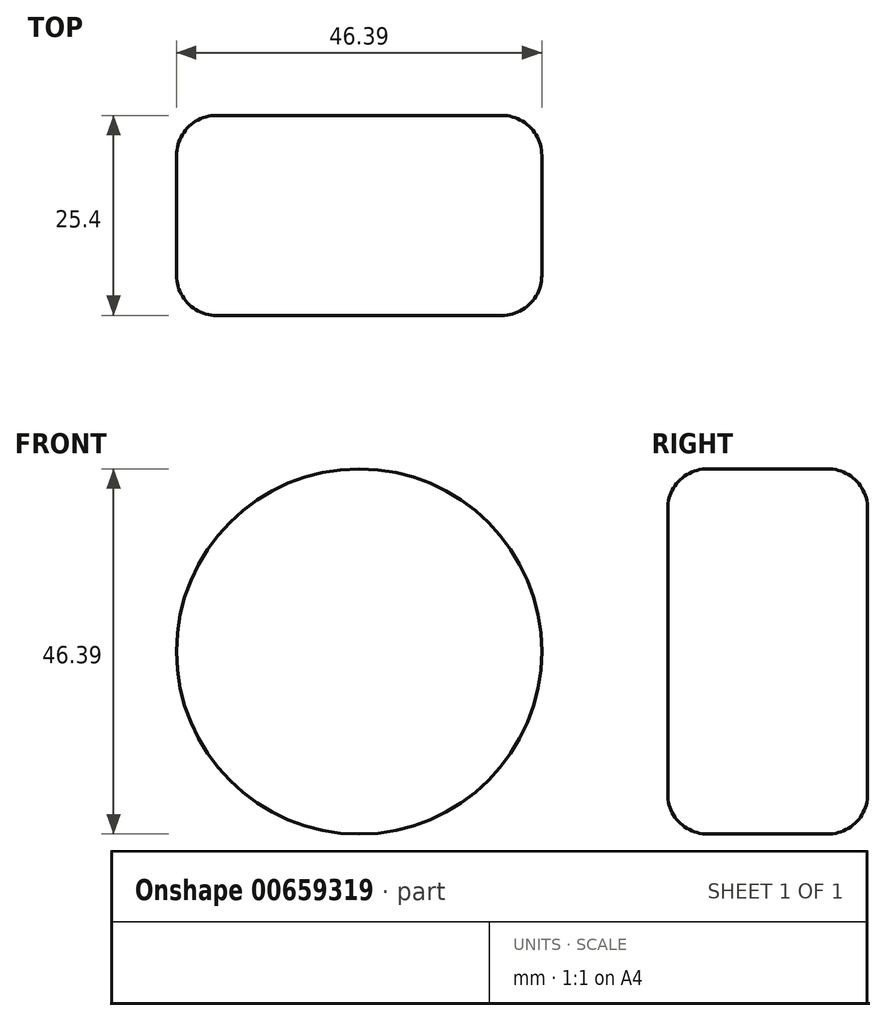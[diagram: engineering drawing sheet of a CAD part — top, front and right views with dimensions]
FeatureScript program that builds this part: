
annotation { "Feature Type Name" : "Feature", "Feature Type Description" : "" }
export const myFeature = defineFeature(function(context is Context, id is Id, definition is map)
    precondition{}
    {
        {
            var Q0;
            Q0=qCreatedBy(makeId("Front.planeOp"),FACE);
            var sketch = newSketch(context, id + "F0", { "sketchPlane" : qUnion([Q0])});
            skCircle(sketch, "E0", {"center": v(-16.93, -16.93) * mm, "radius": 23.2 * mm});
            skSolve(sketch);
        }
        {
            var Q0;
            Q0=makeQuery(id+"F0.imprint","IMPRINT",FACE,{"disambiguationData":[TD([[makeQuery(id+"F0.imprint","IMPRINT",EDGE,{"derivedFrom":sQuery(id+"F0.wireOp",EDGE,"E0")}),1.0]])]});
            extrude(context, id + "F1", {"entities" : qUnion([Q0]), "depth" : 12.7 * mm, "offsetDistance" : 25.4 * mm});
        }
        {
            var Q0;
            Q0=makeQuery(id+"F1.opExtrude","CAP_FACE",FACE,{"disambiguationData":[OSD([sQuery(id+"F0.wireOp",EDGE,"E0")])],"isStart":true});
            var sketch = newSketch(context, id + "F2", { "sketchPlane" : qUnion([Q0])});
            skSolve(sketch);
        }
        {
            var Q0;
            Q0 = qSketchRegion(id + "F2", true);
            var Q1;
            Q1=makeQuery(id+"F2.imprint","IMPRINT",FACE,{"disambiguationData":[TD([[makeQuery(id+"F2.imprint","IMPRINT",EDGE,{"derivedFrom":makeQuery(id+"F1.opExtrude","CAP_EDGE",EDGE,{"disambiguationData":[OSD([sQuery(id+"F0.wireOp",EDGE,"E0")])],"isStart":true})}),-1.0]])]});
            extrude(context, id + "F3", {"entities" : qUnion([Q0, Q1]), "operationType" : NewBodyOperationType.ADD, "depth" : 12.7 * mm, "offsetDistance" : 25.4 * mm});
        }
        {
            var Q0;
            Q0=makeQuery(id+"F3.opExtrude","CAP_FACE",FACE,{"disambiguationData":[OSD([sQuery(id+"F0.wireOp",EDGE,"E0")])],"isStart":false});
            var Q1;
            {var subQ0=sQuery(id+"F0.wireOp",EDGE,"E0");Q1=makeQuery(id+"F3.boolean.opBoolean","MERGE",FACE,{"derivedFrom":[makeQuery(id+"F1.opExtrude","SWEPT_FACE",FACE,{"disambiguationData":[OSD([subQ0])]}),makeQuery(id+"F3.opExtrude","SWEPT_FACE",FACE,{"disambiguationData":[OSD([subQ0])]})]});}
            var Q2;
            Q2=makeQuery(id+"F1.opExtrude","CAP_EDGE",EDGE,{"disambiguationData":[OSD([sQuery(id+"F0.wireOp",EDGE,"E0")])],"isStart":false});
            var Q3;
            Q3=makeQuery(id+"F3.opExtrude","CAP_EDGE",EDGE,{"disambiguationData":[OSD([sQuery(id+"F0.wireOp",EDGE,"E0")])],"isStart":false});
            var Q4;
            Q4=makeQuery(id+"F1.opExtrude","CAP_FACE",FACE,{"disambiguationData":[OSD([sQuery(id+"F0.wireOp",EDGE,"E0")])],"isStart":false});
            fillet(context, id + "F4", {"entities" : qUnion([Q0, Q1, Q2, Q3, Q4]), "radius" : 5.08 * mm, "tangentPropagation" : true, "allowEdgeOverflow" : false});
        }
    });
